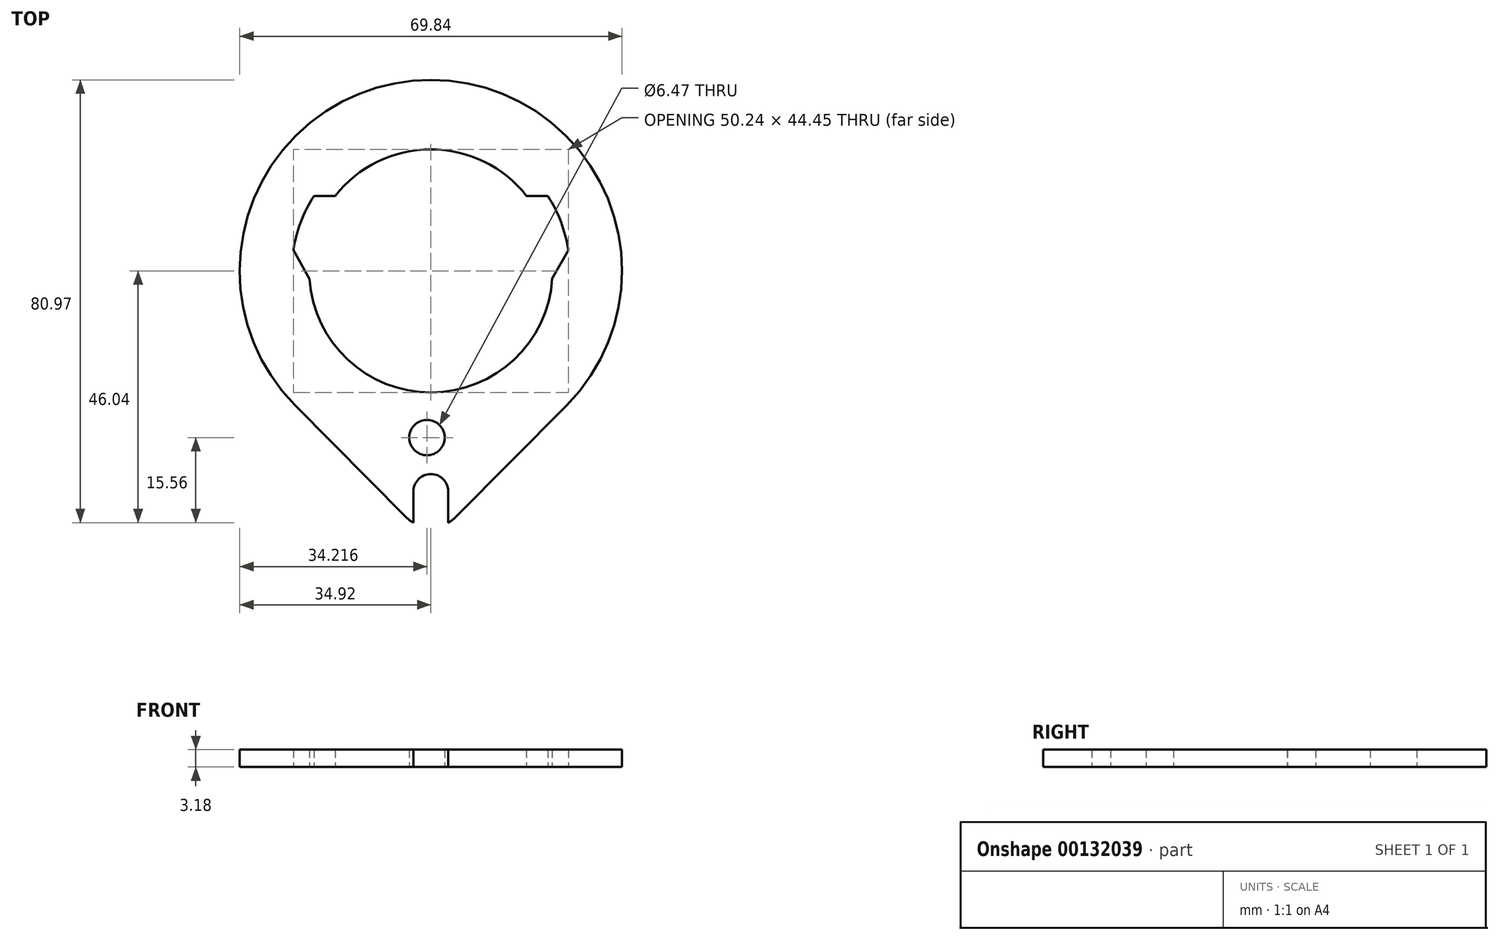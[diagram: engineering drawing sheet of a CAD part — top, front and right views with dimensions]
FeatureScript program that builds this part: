
annotation { "Feature Type Name" : "Feature", "Feature Type Description" : "" }
export const myFeature = defineFeature(function(context is Context, id is Id, definition is map)
    precondition{}
    {
        {
            var Q0;
            Q0=qCreatedBy(makeId("Top.planeOp"),FACE);
            var sketch = newSketch(context, id + "F0", { "sketchPlane" : qUnion([Q0])});
            skArc(sketch, "E0", {"start": v(-22.18, -1.47) * mm, "mid": v(0.03, -22.22) * mm, "end": v(22.18, -1.4) * mm});
            skArc(sketch, "E1", {"start": v(24.76, -24.63) * mm, "mid": v(0.03, 34.92) * mm, "end": v(-24.8, -24.59) * mm});
            skArc(sketch, "E2", {"start": v(3.18, -40.3) * mm, "mid": v(0, -37.13) * mm, "end": v(-3.18, -40.3) * mm});
            skArc(sketch, "E3", {"start": v(-4.65, -44.92) * mm, "mid": v(-3.95, -45.53) * mm, "end": v(-3.18, -46.04) * mm});
            skLineSegment(sketch, "E4", {"start": v(24.7, -24.7) * mm, "end": v(4.65, -44.92) * mm});
            skLineSegment(sketch, "E5", {"start": v(-24.8, -24.59) * mm, "end": v(-4.65, -44.92) * mm});
            skLineSegment(sketch, "E6", {"start": v(-3.18, -40.3) * mm, "end": v(-3.18, -46.04) * mm});
            skLineSegment(sketch, "E7", {"start": v(3.18, -40.3) * mm, "end": v(3.18, -46.04) * mm});
            skArc(sketch, "E8.trimOffspring", {"start": v(3.18, -46.04) * mm, "mid": v(3.95, -45.53) * mm, "end": v(4.65, -44.92) * mm});
            skLineSegment(sketch, "E9", {"start": v(24.7, -24.7) * mm, "end": v(24.76, -24.63) * mm});
            skArc(sketch, "E10", {"start": v(-21.37, 13.72) * mm, "mid": v(-23.77, 8.95) * mm, "end": v(-25.12, 3.77) * mm});
            skLineSegment(sketch, "E11.trimOffspring", {"start": v(17.48, 13.72) * mm, "end": v(21.37, 13.72) * mm});
            skLineSegment(sketch, "E12", {"start": v(-17.48, 13.72) * mm, "end": v(-21.37, 13.72) * mm});
            skLineSegment(sketch, "E13", {"start": v(22.18, -1.4) * mm, "end": v(25.12, 3.77) * mm});
            skArc(sketch, "E14.trimOffspring", {"start": v(25.12, 3.77) * mm, "mid": v(23.77, 8.95) * mm, "end": v(21.37, 13.72) * mm});
            skArc(sketch, "E15.trimOffspring", {"start": v(17.48, 13.72) * mm, "mid": v(0, 22.23) * mm, "end": v(-17.48, 13.72) * mm});
            skCircle(sketch, "E16", {"center": v(-0.7, -30.48) * mm, "radius": 3.23 * mm});
            skPoint(sketch, "E16.centerSnap0", {"position": v(-0.7, -22.21) * mm});
            skLineSegment(sketch, "E17", {"start": v(-25.12, 3.77) * mm, "end": v(-22.18, -1.47) * mm});
            skSolve(sketch);
        }
        {
            var Q0;
            Q0=makeQuery(id+"F0.imprint","IMPRINT",FACE,{"disambiguationData":[TD([[makeQuery(id+"F0.imprint","IMPRINT",EDGE,{"derivedFrom":sQuery(id+"F0.wireOp",EDGE,"E0")}),-1.0]])]});
            extrude(context, id + "F1", {"entities" : qUnion([Q0]), "depth" : 3.17 * mm});
        }
    });
